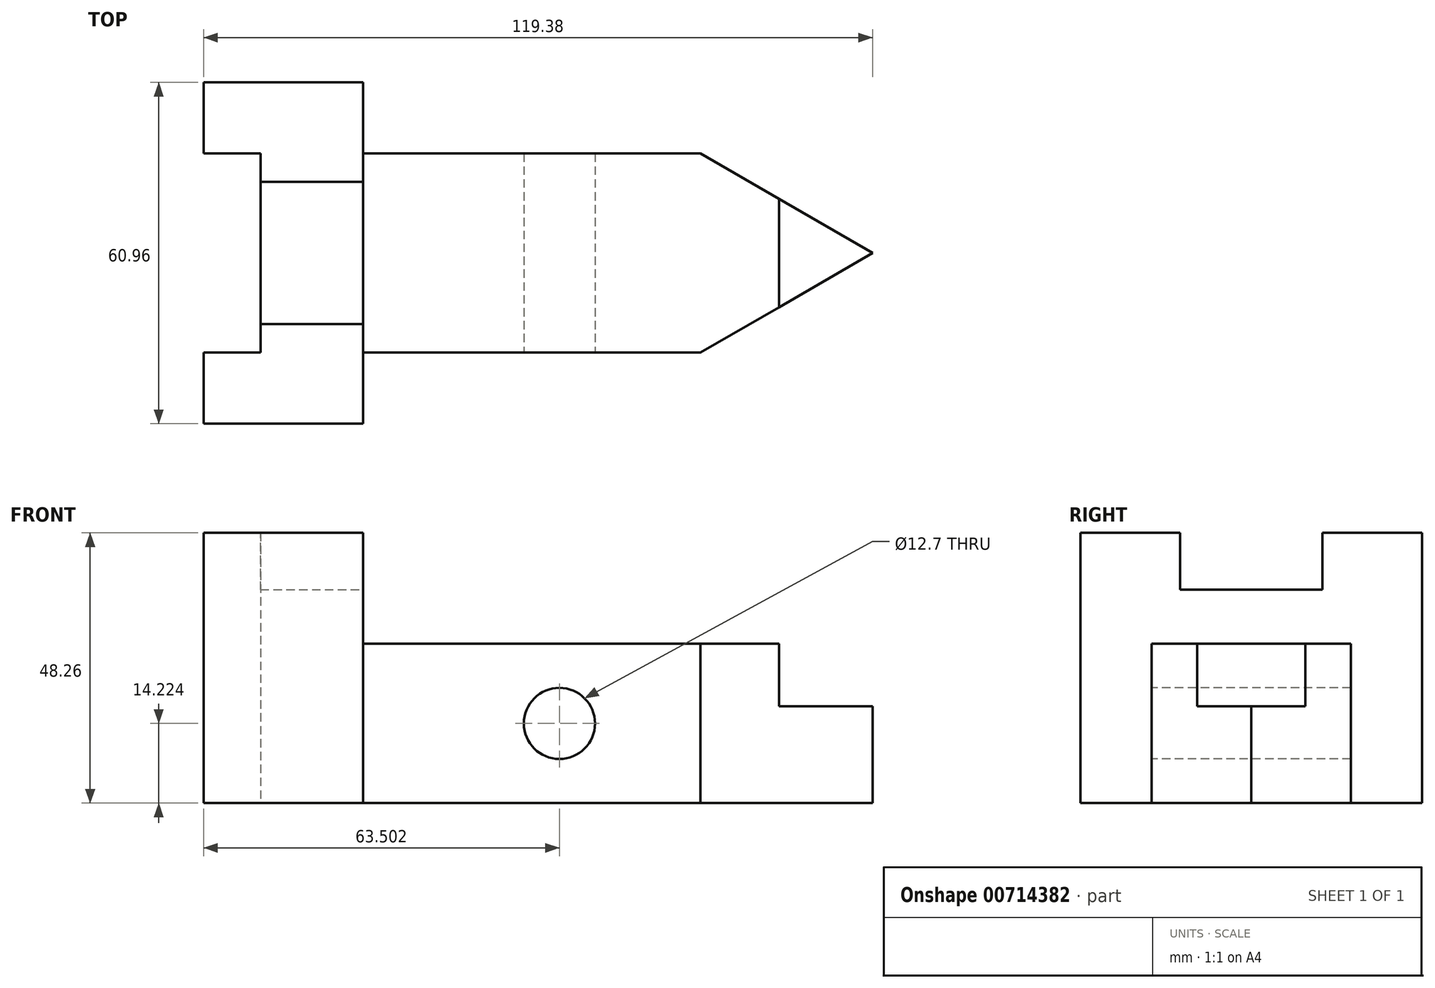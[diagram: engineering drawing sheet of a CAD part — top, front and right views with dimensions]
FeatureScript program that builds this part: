
annotation { "Feature Type Name" : "Feature", "Feature Type Description" : "" }
export const myFeature = defineFeature(function(context is Context, id is Id, definition is map)
    precondition{}
    {
        {
            var Q0;
            Q0=qCreatedBy(makeId("Top.planeOp"),FACE);
            var sketch = newSketch(context, id + "F0", { "sketchPlane" : qUnion([Q0])});
            skLineSegment(sketch, "E0", {"start": v(0, 0) * mm, "end": v(-28.45, 0) * mm});
            skLineSegment(sketch, "E1", {"start": v(-28.45, 0) * mm, "end": v(-28.45, 12.7) * mm});
            skLineSegment(sketch, "E2", {"start": v(-28.45, 12.7) * mm, "end": v(-18.29, 12.7) * mm});
            skLineSegment(sketch, "E3", {"start": v(-18.29, 12.7) * mm, "end": v(-18.29, 17.78) * mm});
            skLineSegment(sketch, "E4", {"start": v(0, 0) * mm, "end": v(0, 30.48) * mm});
            skLineSegment(sketch, "E5", {"start": v(-18.29, 30.48) * mm, "end": v(-18.29, 12.7) * mm});
            skLineSegment(sketch, "E6.MirrorCS", {"start": v(-18.29, 30.48) * mm, "end": v(-18.29, 48.26) * mm});
            skLineSegment(sketch, "E7.MirrorCS", {"start": v(-28.45, 60.96) * mm, "end": v(-28.45, 48.26) * mm});
            skLineSegment(sketch, "E8.MirrorCS", {"start": v(-28.45, 48.26) * mm, "end": v(-18.29, 48.26) * mm});
            skLineSegment(sketch, "E9.MirrorCS", {"start": v(0, 60.96) * mm, "end": v(-28.45, 60.96) * mm});
            skLineSegment(sketch, "E10.MirrorCS", {"start": v(0, 60.96) * mm, "end": v(0, 30.48) * mm});
            skSolve(sketch);
        }
        {
            var Q0;
            Q0 = qSketchRegion(id + "F0", true);
            extrude(context, id + "F1", {"entities" : qUnion([Q0]), "depth" : 48.26 * mm, "offsetDistance" : 25.4 * mm});
        }
        {
            var Q0;
            Q0=makeQuery(id+"F1.opExtrude","SWEPT_FACE",FACE,{"disambiguationData":[OSD([sQuery(id+"F0.wireOp",EDGE,"E4"),sQuery(id+"F0.wireOp",EDGE,"E10.MirrorCS")])]});
            var sketch = newSketch(context, id + "F2", { "sketchPlane" : qUnion([Q0])});
            skLineSegment(sketch, "E11", {"start": v(30.48, 38.1) * mm, "end": v(17.78, 38.1) * mm});
            skLineSegment(sketch, "E12", {"start": v(17.78, 38.1) * mm, "end": v(17.78, 48.26) * mm});
            skLineSegment(sketch, "E13", {"start": v(17.78, 48.26) * mm, "end": v(43.18, 48.26) * mm});
            skLineSegment(sketch, "E14", {"start": v(43.18, 48.26) * mm, "end": v(43.18, 38.1) * mm});
            skLineSegment(sketch, "E15", {"start": v(43.18, 38.1) * mm, "end": v(30.48, 38.1) * mm});
            skSolve(sketch);
        }
        {
            var Q0;
            Q0 = qSketchRegion(id + "F2", true);
            extrude(context, id + "F3", {"entities" : qUnion([Q0]), "operationType" : NewBodyOperationType.REMOVE, "endBound" : BoundingType.UP_TO_NEXT, "oppositeDirection" : true, "depth" : 25.4 * mm, "offsetDistance" : 25.4 * mm});
        }
        {
            var Q0;
            Q0=qCreatedBy(makeId("Top.planeOp"),FACE);
            var sketch = newSketch(context, id + "F4", { "sketchPlane" : qUnion([Q0])});
            skLineSegment(sketch, "E16", {"start": v(0, 0) * mm, "end": v(0, 30.48) * mm});
            skLineSegment(sketch, "E17", {"start": v(0, 30.48) * mm, "end": v(0, 48.26) * mm});
            skLineSegment(sketch, "E18", {"start": v(0, 48.26) * mm, "end": v(60.2, 48.26) * mm});
            skLineSegment(sketch, "E19", {"start": v(60.2, 48.26) * mm, "end": v(90.93, 30.48) * mm});
            skLineSegment(sketch, "E20.MirrorCS", {"start": v(0, 30.48) * mm, "end": v(0, 12.7) * mm});
            skLineSegment(sketch, "E21.MirrorCS", {"start": v(0, 12.7) * mm, "end": v(60.2, 12.7) * mm});
            skLineSegment(sketch, "E22.MirrorCS", {"start": v(60.2, 12.7) * mm, "end": v(90.93, 30.48) * mm});
            skSolve(sketch);
        }
        {
            var Q0;
            Q0 = qSketchRegion(id + "F4", true);
            extrude(context, id + "F5", {"entities" : qUnion([Q0]), "operationType" : NewBodyOperationType.ADD, "depth" : 28.45 * mm, "offsetDistance" : 25.4 * mm});
        }
        {
            var Q0;
            Q0=makeQuery(id+"F5.opExtrude","CAP_FACE",FACE,{"disambiguationData":[OSD([sQuery(id+"F4.wireOp",EDGE,"E17"),sQuery(id+"F4.wireOp",EDGE,"E18"),sQuery(id+"F4.wireOp",EDGE,"E19"),sQuery(id+"F4.wireOp",EDGE,"E20.MirrorCS"),sQuery(id+"F4.wireOp",EDGE,"E21.MirrorCS"),sQuery(id+"F4.wireOp",EDGE,"E22.MirrorCS")])],"isStart":false});
            var sketch = newSketch(context, id + "F6", { "sketchPlane" : qUnion([Q0])});
            skLineSegment(sketch, "E23", {"start": v(90.93, 30.48) * mm, "end": v(74.22, 40.15) * mm});
            skLineSegment(sketch, "E24", {"start": v(74.22, 40.15) * mm, "end": v(74.22, 20.81) * mm});
            skLineSegment(sketch, "E25", {"start": v(74.22, 20.81) * mm, "end": v(90.93, 30.48) * mm});
            skSolve(sketch);
        }
        {
            var Q0;
            Q0 = qSketchRegion(id + "F6", true);
            extrude(context, id + "F7", {"entities" : qUnion([Q0]), "operationType" : NewBodyOperationType.REMOVE, "oppositeDirection" : true, "depth" : 11.18 * mm, "offsetDistance" : 25.4 * mm});
        }
        {
            var Q0;
            Q0=makeQuery(id+"F5.opExtrude","SWEPT_FACE",FACE,{"disambiguationData":[OSD([sQuery(id+"F4.wireOp",EDGE,"E21.MirrorCS")])]});
            var sketch = newSketch(context, id + "F8", { "sketchPlane" : qUnion([Q0])});
            skCircle(sketch, "E26", {"center": v(35.05, 14.22) * mm, "radius": 6.35 * mm});
            skSolve(sketch);
        }
        {
            var Q0;
            Q0 = qSketchRegion(id + "F8", true);
            extrude(context, id + "F9", {"entities" : qUnion([Q0]), "operationType" : NewBodyOperationType.REMOVE, "endBound" : BoundingType.UP_TO_NEXT, "oppositeDirection" : true, "depth" : 25.4 * mm, "offsetDistance" : 25.4 * mm});
        }
    });
